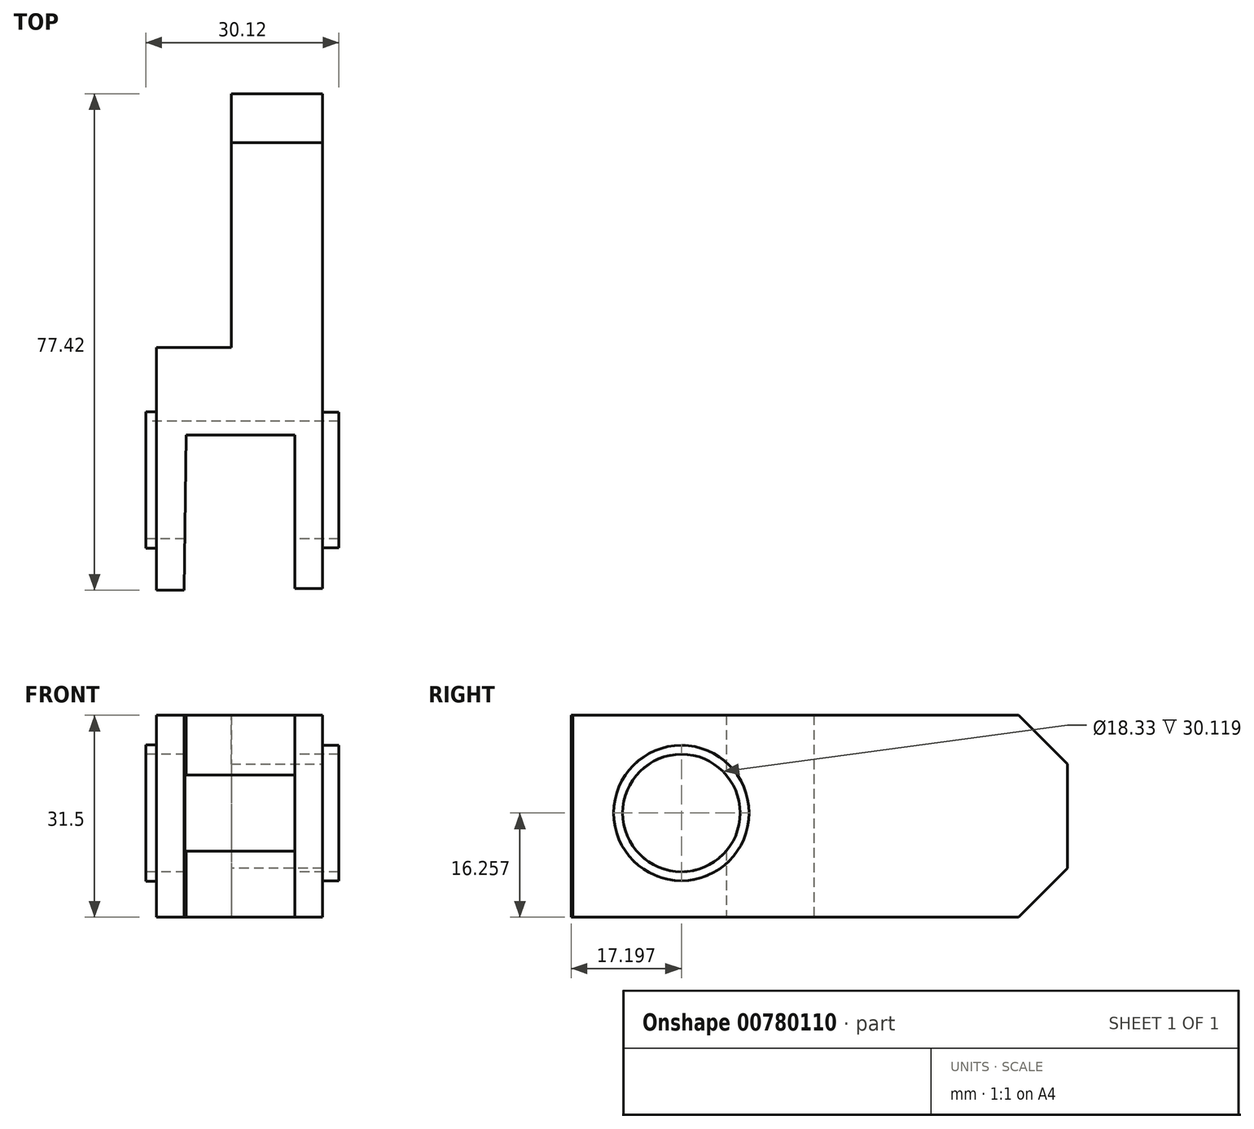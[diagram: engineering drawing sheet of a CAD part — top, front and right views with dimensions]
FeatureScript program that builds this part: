
annotation { "Feature Type Name" : "Feature", "Feature Type Description" : "" }
export const myFeature = defineFeature(function(context is Context, id is Id, definition is map)
    precondition{}
    {
        {
            var Q0;
            Q0=qCreatedBy(makeId("Top.planeOp"),FACE);
            var sketch = newSketch(context, id + "F0", { "sketchPlane" : qUnion([Q0])});
            skLineSegment(sketch, "E0", {"start": v(0, 0) * mm, "end": v(-11.66, 0) * mm});
            skLineSegment(sketch, "E1", {"start": v(0, 0) * mm, "end": v(0, 39.57) * mm});
            skLineSegment(sketch, "E2", {"start": v(0, 39.57) * mm, "end": v(14.25, 39.57) * mm});
            skLineSegment(sketch, "E3", {"start": v(14.25, 39.57) * mm, "end": v(14.25, 0) * mm});
            skLineSegment(sketch, "E4", {"start": v(14.25, 0) * mm, "end": v(14.25, -37.56) * mm});
            skLineSegment(sketch, "E5", {"start": v(14.25, -37.56) * mm, "end": v(9.93, -37.56) * mm});
            skLineSegment(sketch, "E6", {"start": v(9.93, -37.56) * mm, "end": v(9.93, -13.67) * mm});
            skLineSegment(sketch, "E7", {"start": v(9.93, -13.67) * mm, "end": v(-7.05, -13.67) * mm});
            skLineSegment(sketch, "E8", {"start": v(-11.66, 0) * mm, "end": v(-11.66, -37.85) * mm});
            skLineSegment(sketch, "E9", {"start": v(-11.66, -37.85) * mm, "end": v(-7.34, -37.85) * mm});
            skLineSegment(sketch, "E10", {"start": v(-7.34, -37.85) * mm, "end": v(-7.05, -13.67) * mm});
            skSolve(sketch);
        }
        {
            var Q0;
            Q0=makeQuery(id+"F0.imprint","IMPRINT",FACE,{"disambiguationData":[TD([[makeQuery(id+"F0.imprint","IMPRINT",EDGE,{"derivedFrom":sQuery(id+"F0.wireOp",EDGE,"E0")}),1.0]])]});
            extrude(context, id + "F1", {"entities" : qUnion([Q0]), "depth" : 31.5 * mm, "offsetDistance" : 25.4 * mm});
        }
        {
            var Q0;
            Q0=makeQuery(id+"F1.opExtrude","SWEPT_FACE",FACE,{"disambiguationData":[OSD([sQuery(id+"F0.wireOp",EDGE,"E8")])]});
            var sketch = newSketch(context, id + "F2", { "sketchPlane" : qUnion([Q0])});
            skCircle(sketch, "E11", {"center": v(20.65, 16.26) * mm, "radius": 10.63 * mm});
            skCircle(sketch, "E12", {"center": v(20.65, 16.26) * mm, "radius": 9.17 * mm});
            skSolve(sketch);
        }
        {
            var Q0;
            Q0=makeQuery(id+"F1.opExtrude","CAP_EDGE",EDGE,{"disambiguationData":[OSD([sQuery(id+"F0.wireOp",EDGE,"E2")])],"isStart":false});
            var Q1;
            Q1=makeQuery(id+"F1.opExtrude","CAP_EDGE",EDGE,{"disambiguationData":[OSD([sQuery(id+"F0.wireOp",EDGE,"E2")])],"isStart":true});
            chamfer(context, id + "F3", {"entities" : qUnion([Q0, Q1]), "width" : 7.62 * mm, "tangentPropagation" : true});
        }
        {
            var Q0;
            Q0=makeQuery(id+"F2.imprint","IMPRINT",FACE,{"disambiguationData":[TD([[makeQuery(id+"F2.imprint","IMPRINT",EDGE,{"derivedFrom":sQuery(id+"F2.wireOp",EDGE,"E12")}),1.0]])]});
            extrude(context, id + "F4", {"entities" : qUnion([Q0]), "operationType" : NewBodyOperationType.REMOVE, "endBound" : BoundingType.THROUGH_ALL, "oppositeDirection" : true, "depth" : 25.4 * mm, "offsetDistance" : 25.4 * mm});
        }
        {
            var Q0;
            Q0=makeQuery(id+"F2.imprint","IMPRINT",FACE,{"disambiguationData":[TD([[makeQuery(id+"F2.imprint","IMPRINT",EDGE,{"derivedFrom":sQuery(id+"F2.wireOp",EDGE,"E11")}),1.0]])]});
            extrude(context, id + "F5", {"entities" : qUnion([Q0]), "operationType" : NewBodyOperationType.ADD, "depth" : 1.68 * mm, "offsetDistance" : 25.4 * mm});
        }
        {
            var Q0;
            Q0=makeQuery(id+"F1.opExtrude","SWEPT_FACE",FACE,{"disambiguationData":[OSD([sQuery(id+"F0.wireOp",EDGE,"E3"),sQuery(id+"F0.wireOp",EDGE,"E4")])]});
            var sketch = newSketch(context, id + "F6", { "sketchPlane" : qUnion([Q0])});
            skCircle(sketch, "E13", {"center": v(-20.65, 16.26) * mm, "radius": 10.55 * mm});
            skSolve(sketch);
        }
        {
            var Q0;
            Q0=makeQuery(id+"F6.imprint","IMPRINT",FACE,{"disambiguationData":[TD([[makeQuery(id+"F6.imprint","IMPRINT",EDGE,{"derivedFrom":sQuery(id+"F6.wireOp",EDGE,"E13")}),1.0]])]});
            extrude(context, id + "F7", {"entities" : qUnion([Q0]), "operationType" : NewBodyOperationType.ADD, "depth" : 2.54 * mm, "offsetDistance" : 25.4 * mm});
        }
    });
